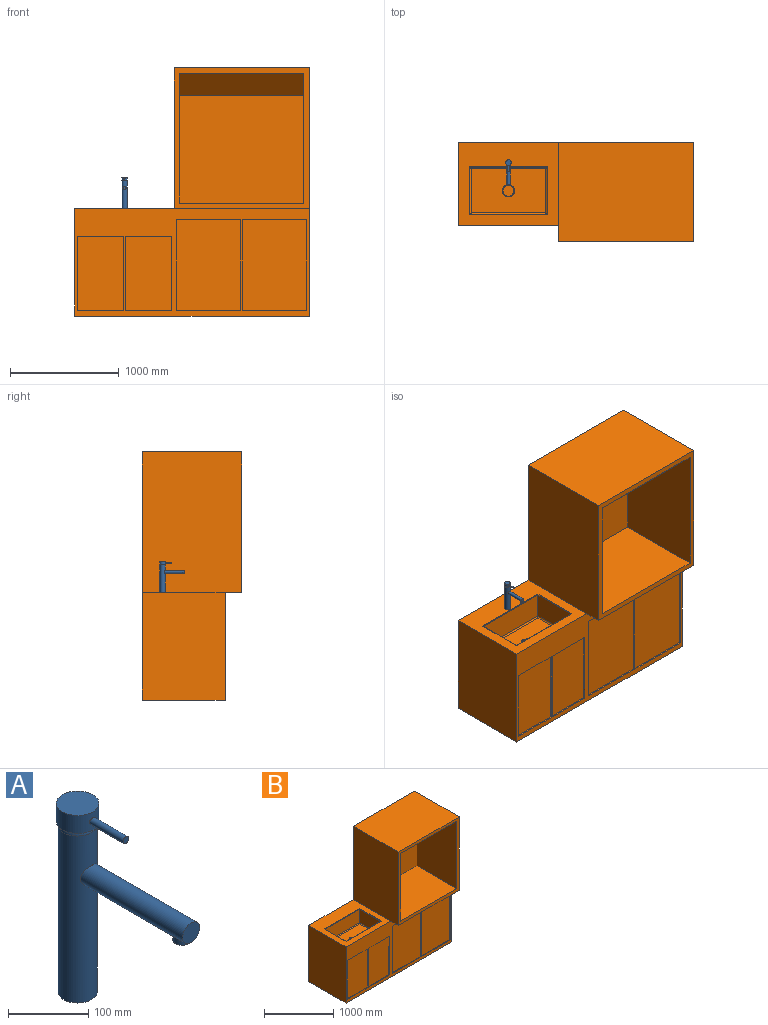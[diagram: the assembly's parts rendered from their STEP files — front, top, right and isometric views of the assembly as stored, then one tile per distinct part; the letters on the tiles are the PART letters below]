
ASSEMBLY  parts=2 mates=1
PART A: 12 faces, bbox 53x226.5x287.8 mm
  f0: cylinder r=24.5mm len=255mm, axis (0,0,-1), area 38509.1mm2, adj f2,f3,f8
  f1: cylinder r=26.5mm len=53mm, axis (0,0,-1), area 4499.8mm2, adj f4,f5,f6
  f2: torus R=10.5mm, axis (0,0,1), area 816.9mm2, adj f0,f5
  f3: plane 49x49mm, normal (0,0,-1), area 1885.7mm2, adj f0
  f4: plane 53x53mm, normal (0,0,1), area 2206.2mm2, adj f1
  f5: plane 53x53mm, normal (0,0,-1), area 474.4mm2, adj f1,f2
  f6: cylinder r=5mm len=58.98mm, axis (0,1,0), area 1845.3mm2, adj f1,f7
  f7: plane 10x10mm, normal (0,-1,0), area 78.5mm2, adj f6
  f8: cylinder r=15mm len=180.63mm, axis (0,1,0), area 16273mm2, adj f0,f9,f10
  f9: plane 30x30mm, normal (0,-1,0), area 706.9mm2, adj f8
  f10: cylinder r=12mm len=24mm, axis (0,0,1), area 476.2mm2, adj f8,f11
  f11: plane 24x24mm, normal (0,0,-1), area 452.4mm2, adj f10
PART B: 52 faces, bbox 2159x914.4x2286 mm
  f0: plane 2159x990.6mm, normal (0,-1,0), area 565160.2mm2, adj f2,f4,f6,f24,f25,f32,f33,f34
  f1: plane 1295.4x1244.6mm, normal (0,-1,0), area 247741.4mm2, adj f5,f23,f24,f25,f26,f27,f28,f31
  f2: plane 914.4x762mm, normal (0,0,1), area 377960.5mm2, adj f0,f3,f5,f6,f12,f13,f14,f15
  f3: plane 2286x2159mm, normal (0,1,0), area 3750960.2mm2, adj f2,f4,f5,f6,f23,f25
  f4: plane 2159x762mm, normal (0,0,-1), area 1645158mm2, adj f0,f3,f6,f25
  f5: plane 1295.4x914.4mm, normal (-1,0,0), area 1184513.8mm2, adj f1,f2,f3,f23,f24
  f6: plane 990.6x762mm, normal (-1,0,0), area 754837.2mm2, adj f0,f2,f3,f4
  f7: plane 711.2x236.22mm, normal (0,-1,0), area 167999.7mm2, adj f8,f10,f12,f16
  f8: plane 431.8x236.22mm, normal (1,0,0), area 101999.8mm2, adj f7,f9,f13,f17
  f9: plane 711.2x236.22mm, normal (0,1,0), area 167999.7mm2, adj f8,f10,f15,f19
  f10: plane 431.8x236.22mm, normal (-1,0,0), area 101999.8mm2, adj f7,f9,f14,f18
  f11: plane 685.8x406.4mm, normal (0,0,1), area 268448.3mm2, adj f16,f17,f18,f19,f22
  f12: cylinder r=5.08mm len=721.36mm, axis (-1,0,0), area 5704.6mm2, adj f2,f7,f13,f14
  f13: cylinder r=5.08mm len=441.96mm, axis (0,-1,0), area 3475.1mm2, adj f2,f8,f12,f15
  f14: cylinder r=5.08mm len=441.96mm, axis (0,1,0), area 3475.1mm2, adj f2,f10,f12,f15
  f15: cylinder r=5.08mm len=721.36mm, axis (1,0,0), area 5704.6mm2, adj f2,f9,f13,f14
  f16: cylinder r=12.7mm len=711.2mm, axis (-1,0,0), area 14003.7mm2, adj f7,f11,f17,f18
  f17: cylinder r=12.7mm len=431.8mm, axis (0,-1,0), area 8429.9mm2, adj f8,f11,f16,f19
  f18: cylinder r=12.7mm len=431.8mm, axis (0,1,0), area 8429.9mm2, adj f10,f11,f16,f19
  f19: cylinder r=12.7mm len=711.2mm, axis (1,0,0), area 14003.7mm2, adj f9,f11,f17,f18
  f20: cylinder r=50.8mm len=120.65mm, axis (0,0,1), area 38509.8mm2, adj f21,f22
  f21: plane 101.6x101.6mm, normal (0,0,1), area 8107.3mm2, adj f20
  f22: torus R=57.15mm, axis (0,0,1), area 3328.4mm2, adj f11,f20
  f23: plane 1244.6x914.4mm, normal (0,0,1), area 1138062.2mm2, adj f1,f3,f5,f25
  f24: plane 1244.6x152.4mm, normal (0,0,-1), area 189677mm2, adj f0,f1,f5,f25
  f25: plane 2286x914.4mm, normal (1,0,0), area 1939351mm2, adj f0,f1,f3,f4,f23,f24
  f26: plane 1193.8x812.8mm, normal (1,0,0), area 825804.8mm2, adj f1,f27,f29,f30,f31
  f27: plane 1143x812.8mm, normal (0,0,1), area 929030.4mm2, adj f1,f26,f28,f30
  f28: plane 1193.8x812.8mm, normal (-1,0,0), area 825804.8mm2, adj f1,f27,f29,f30,f31
  f29: plane 1143x609.6mm, normal (0,0,-1), area 696772.8mm2, adj f26,f28,f30,f31
  f30: plane 1143x990.6mm, normal (0,-1,0), area 1132255.8mm2, adj f26,f27,f28,f29
  f31: plane 1143x203.2mm, normal (0,-0.71,-0.71), area 328461.8mm2, adj f1,f26,f28,f29
  f32: plane 590.55x12.7mm, normal (0,0,-1), area 7500mm2, adj f0,f33,f35,f36
  f33: plane 838.2x12.7mm, normal (1,0,0), area 10645.1mm2, adj f0,f32,f34,f36
  f34: plane 590.55x12.7mm, normal (0,0,1), area 7500mm2, adj f0,f33,f35,f36
  f35: plane 838.2x12.7mm, normal (-1,0,0), area 10645.1mm2, adj f0,f32,f34,f36
  f36: plane 838.2x590.55mm, normal (0,-1,0), area 494999mm2, adj f32,f33,f34,f35
  f37: plane 590.55x12.7mm, normal (0,0,-1), area 7500mm2, adj f0,f38,f40,f41
  f38: plane 838.2x12.7mm, normal (1,0,0), area 10645.1mm2, adj f0,f37,f39,f41
  f39: plane 590.55x12.7mm, normal (0,0,1), area 7500mm2, adj f0,f38,f40,f41
  f40: plane 838.2x12.7mm, normal (-1,0,0), area 10645.1mm2, adj f0,f37,f39,f41
  f41: plane 838.2x590.55mm, normal (0,-1,0), area 494999mm2, adj f37,f38,f39,f40
  f42: plane 425.45x12.7mm, normal (0,0,-1), area 5403.2mm2, adj f0,f43,f45,f46
  f43: plane 685.8x12.7mm, normal (1,0,0), area 8709.7mm2, adj f0,f42,f44,f46
  f44: plane 425.45x12.7mm, normal (0,0,1), area 5403.2mm2, adj f0,f43,f45,f46
  f45: plane 685.8x12.7mm, normal (-1,0,0), area 8709.7mm2, adj f0,f42,f44,f46
  f46: plane 685.8x425.45mm, normal (0,-1,0), area 291773.6mm2, adj f42,f43,f44,f45
  f47: plane 425.45x12.7mm, normal (0,0,-1), area 5403.2mm2, adj f0,f48,f50,f51
  f48: plane 685.8x12.7mm, normal (1,0,0), area 8709.7mm2, adj f0,f47,f49,f51
  f49: plane 425.45x12.7mm, normal (0,0,1), area 5403.2mm2, adj f0,f48,f50,f51
  f50: plane 685.8x12.7mm, normal (-1,0,0), area 8709.7mm2, adj f0,f47,f49,f51
  f51: plane 685.8x425.45mm, normal (0,-1,0), area 291773.6mm2, adj f47,f48,f49,f50
PLACE A t=(266.62,-77.94,757.94)mm
PLACE B t=(876.22,-273.52,-232.66)mm
MATE fastened A.f0 <-> B.f2  axis (0,0,-1) through (266.62,-77.94,757.94)mm
